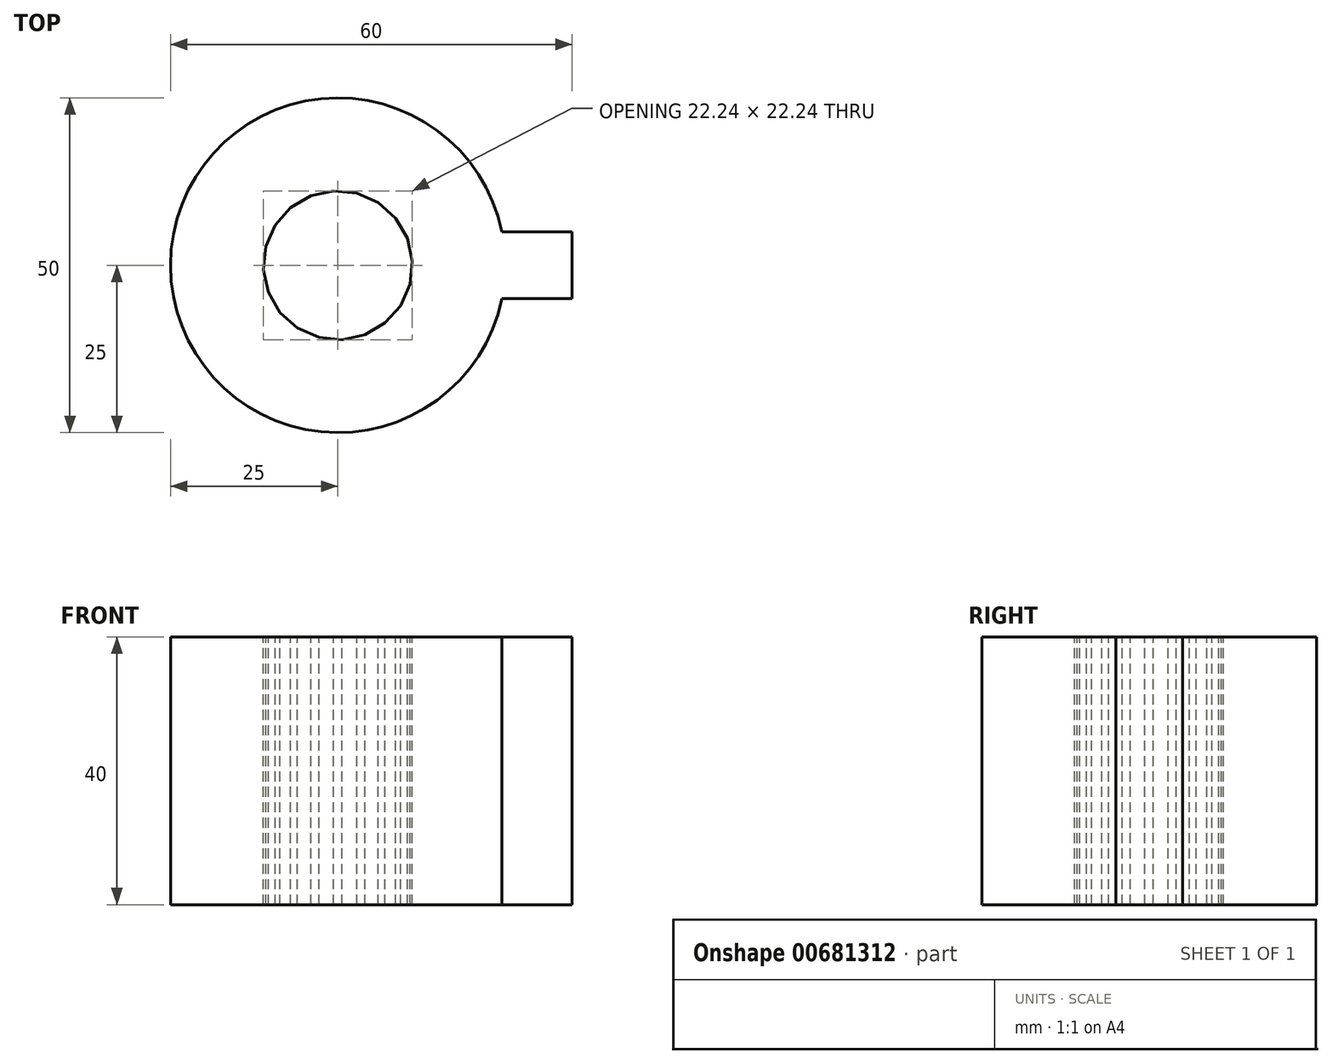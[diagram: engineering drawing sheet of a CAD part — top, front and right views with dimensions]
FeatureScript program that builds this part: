
annotation { "Feature Type Name" : "Feature", "Feature Type Description" : "" }
export const myFeature = defineFeature(function(context is Context, id is Id, definition is map)
    precondition{}
    {
        {
            var Q0;
            Q0=qCreatedBy(makeId("Top.planeOp"),FACE);
            var sketch = newSketch(context, id + "F0", { "sketchPlane" : qUnion([Q0])});
            skArc(sketch, "E0", {"start": v(24.5, 5) * mm, "mid": v(-25, 0) * mm, "end": v(24.5, -5) * mm});
            skLineSegment(sketch, "E1.bottom", {"start": v(24.5, 5) * mm, "end": v(35, 5) * mm});
            skLineSegment(sketch, "E1.top", {"start": v(24.5, -5) * mm, "end": v(35, -5) * mm});
            skLineSegment(sketch, "E1.right", {"start": v(35, 5) * mm, "end": v(35, -5) * mm});
            skSolve(sketch);
        }
        {
            var Q0;
            Q0=makeQuery(id+"F0.imprint","IMPRINT",FACE,{"disambiguationData":[TD([[makeQuery(id+"F0.imprint","IMPRINT",EDGE,{"derivedFrom":sQuery(id+"F0.wireOp",EDGE,"E0")}),1.0]])]});
            extrude(context, id + "F1", {"entities" : qUnion([Q0]), "depth" : 40 * mm, "offsetDistance" : 25 * mm});
        }
        {
            var Q0;
            Q0=makeQuery(id+"F1.opExtrude","CAP_FACE",FACE,{"disambiguationData":[OSD([sQuery(id+"F0.wireOp",EDGE,"E0"),sQuery(id+"F0.wireOp",EDGE,"E1.bottom"),sQuery(id+"F0.wireOp",EDGE,"E1.top"),sQuery(id+"F0.wireOp",EDGE,"E1.right")])],"isStart":false});
            var sketch = newSketch(context, id + "F2", { "sketchPlane" : qUnion([Q0])});
            skCircle(sketch, "E2.cCircle", {"center": v(0, 0) * mm, "radius": 11 * mm, "construction": true});
            skLineSegment(sketch, "E2.0", {"start": v(-8.62, -7.05) * mm, "end": v(-10.38, -4.04) * mm});
            skLineSegment(sketch, "E2.1", {"start": v(-10.38, -4.04) * mm, "end": v(-11.12, -0.63) * mm});
            skLineSegment(sketch, "E2.2", {"start": v(-11.12, -0.63) * mm, "end": v(-10.77, 2.83) * mm});
            skLineSegment(sketch, "E2.3", {"start": v(-10.77, 2.83) * mm, "end": v(-9.37, 6.02) * mm});
            skLineSegment(sketch, "E2.4", {"start": v(-9.37, 6.02) * mm, "end": v(-7.05, 8.62) * mm});
            skLineSegment(sketch, "E2.5", {"start": v(-7.05, 8.62) * mm, "end": v(-4.04, 10.38) * mm});
            skLineSegment(sketch, "E2.6", {"start": v(-4.04, 10.38) * mm, "end": v(-0.63, 11.12) * mm});
            skLineSegment(sketch, "E2.7", {"start": v(-0.63, 11.12) * mm, "end": v(2.83, 10.77) * mm});
            skLineSegment(sketch, "E2.8", {"start": v(2.83, 10.77) * mm, "end": v(6.02, 9.37) * mm});
            skLineSegment(sketch, "E2.9", {"start": v(6.02, 9.37) * mm, "end": v(8.62, 7.05) * mm});
            skLineSegment(sketch, "E2.10", {"start": v(8.62, 7.05) * mm, "end": v(10.38, 4.04) * mm});
            skLineSegment(sketch, "E2.11", {"start": v(10.38, 4.04) * mm, "end": v(11.12, 0.63) * mm});
            skLineSegment(sketch, "E2.12", {"start": v(11.12, 0.63) * mm, "end": v(10.77, -2.83) * mm});
            skLineSegment(sketch, "E2.13", {"start": v(10.77, -2.83) * mm, "end": v(9.37, -6.02) * mm});
            skLineSegment(sketch, "E2.14", {"start": v(9.37, -6.02) * mm, "end": v(7.05, -8.62) * mm});
            skLineSegment(sketch, "E2.15", {"start": v(7.05, -8.62) * mm, "end": v(4.04, -10.38) * mm});
            skLineSegment(sketch, "E2.16", {"start": v(4.04, -10.38) * mm, "end": v(0.63, -11.12) * mm});
            skLineSegment(sketch, "E2.17", {"start": v(0.63, -11.12) * mm, "end": v(-2.83, -10.77) * mm});
            skLineSegment(sketch, "E2.18", {"start": v(-2.83, -10.77) * mm, "end": v(-6.02, -9.37) * mm});
            skLineSegment(sketch, "E2.19", {"start": v(-6.02, -9.37) * mm, "end": v(-8.62, -7.05) * mm});
            skSolve(sketch);
        }
        {
            var Q0;
            Q0=makeQuery(id+"F2.imprint","IMPRINT",FACE,{"disambiguationData":[TD([[makeQuery(id+"F2.imprint","IMPRINT",EDGE,{"derivedFrom":sQuery(id+"F2.wireOp",EDGE,"E2.0")}),-1.0]])]});
            extrude(context, id + "F3", {"entities" : qUnion([Q0]), "operationType" : NewBodyOperationType.REMOVE, "oppositeDirection" : true, "depth" : 50 * mm, "offsetDistance" : 25 * mm});
        }
    });
